# Revit family: BalizadorConcreto_PBC20W_PowerLume
name_source: partatom
category: Luminárias
units: mm (PartAtom-declared; Revit-internal decimal feet)

## family parameters
Compartilhado = Sim
Corte com vazios quando carregada = Sim
Cota do conector redondo = Utilizar diâmetro
Fonte luminosa = Não
Hospedeiro = Face
Manter orientação da anotação = Não
Número OmniClass = 23.80.70.14.11.14
Ponto de cálculo do ambiente = Não
Tipo de parte = Normal
Título OmniClass = Post-Top Lighting

## types (2) — shared parameters
Carga Aparente Luminária = 0 VA
Catálogo de produtos = https://www.powerlume.com.br
Comentários de voltagem = 110 ou 220Vac 50/60Hz com driver incorporado
Contato do fabricante = (54) 3066-6488
Data da atualização = 27/02/2025
Descrição = Poste balizador LED em concreto
Difusor = PMMA transparente anti UV
Diâmetro do frame = 192 mm  [stored 0.629921 ft]
Elevação-padrão = 1219 mm
Fabricante = Power Lume
Fator de Potência Luminária = 1
Fluxo luminoso = 1715 lm
Fonte luminosa = BalizadorConcreto_PBC20W_FonteLuminosa_PowerLume : 3000K
Frame = Concreto, leve
IP = 65
IRC = 90
IfcExportAs = IfcLightFixtureType
Localização = Caxias do Sul - RS / Brasil
Lâmpada = Placa LED
Peso = 0
Potência = 20W
Temperatura de cor = 3000K
URL = https://www.powerlume.com.br
URL do produto = https://www.powerlume.com.br
Versão = 1
Vida útil = 60000h
Voltagem Luminária = 0 V

## per-type parameters (varying)
| type | Altura | Altura da base | Modelo | Tipo de imagem | Ângulo de abertura |
| PBC20W-P - 540mm | 540 mm  [stored 1.77165 ft] | 377 mm  [stored 1.23688 ft] | PBC20W-P | FOTO PBC20WP.png | 0 |
| PBC20W-G - 990mm | 990 mm  [stored 3.24803 ft] | 827 mm  [stored 2.71325 ft] | PBC20W-G | FOTO PBC20WG.png | Difuso |

note: [stored X ft] marks values corroborated as IEEE doubles in the binary element streams (Revit-internal decimal feet)
